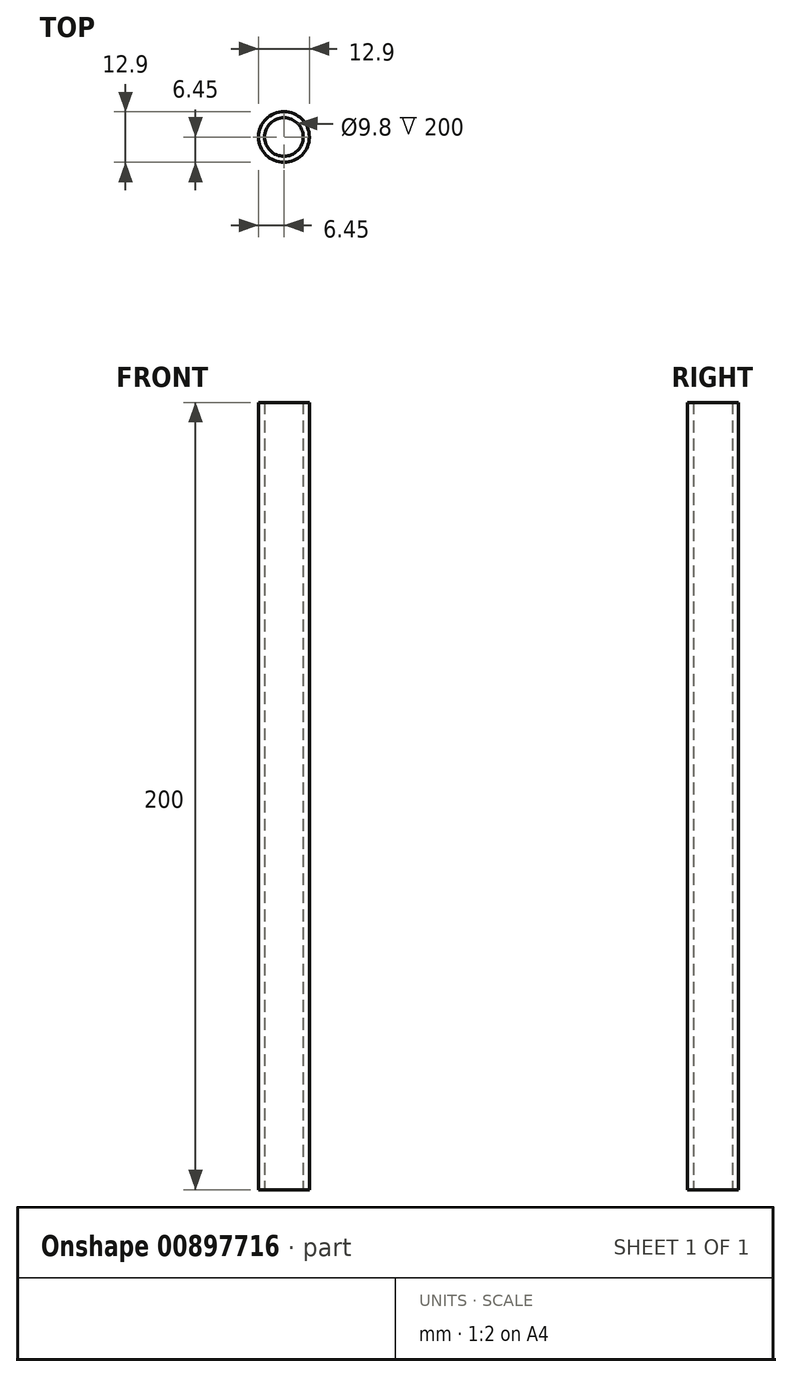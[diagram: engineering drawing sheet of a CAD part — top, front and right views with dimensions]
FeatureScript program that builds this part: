
annotation { "Feature Type Name" : "Feature", "Feature Type Description" : "" }
export const myFeature = defineFeature(function(context is Context, id is Id, definition is map)
    precondition{}
    {
        {
            var Q0;
            Q0=qCreatedBy(makeId("Top.planeOp"),FACE);
            var sketch = newSketch(context, id + "F0", { "sketchPlane" : qUnion([Q0])});
            skCircle(sketch, "E0", {"center": v(0, 0) * mm, "radius": 6.45 * mm});
            skCircle(sketch, "E1", {"center": v(0, 0) * mm, "radius": 4.9 * mm});
            skSolve(sketch);
        }
        {
            var Q0;
            Q0 = qSketchRegion(id + "F0", true);
            extrude(context, id + "F1", {"entities" : qUnion([Q0]), "depth" : 200 * mm, "offsetDistance" : 25 * mm});
        }
    });
